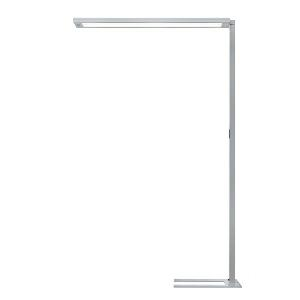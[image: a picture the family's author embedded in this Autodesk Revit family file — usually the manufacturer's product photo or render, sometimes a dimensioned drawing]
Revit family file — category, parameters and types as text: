
# Revit family: lavigo_-_dps_18000_vtl_r_g2_00801138_1d74
name_source: partatom
category: Lighting Fixtures
units: mm (PartAtom-declared; Revit-internal decimal feet)

## family parameters
Cut with Voids When Loaded = No
Host = Face
Light Source = No
Part Type = Normal
Room Calculation Point = No
Round Connector Dimension = Use Diameter
Shared = No

## types (1)
- LAVIGO - DPS 18000/VTL/R/G2 (1 x LED VTL, 18550 lm, 3000-6500K)
    Apparent Load = 128 VA
    Approval mark = CE
    CIE Flux Codes = 60 87 97 9 100
    Color Rendering = 80-89
    Color Temperature = 3000-6500K
    Control Gear = Electronic ballast
    Default Elevation = 1800 mm
    Description = DPS 18000/VTL/R/G2|Free-standing luminaire|light source: LED  3000-6500 K  Energy efficiency category A/A+/A++|LED  4000 K 4000 K Energy efficiency category A/A+/A++|work equipment: Electronic ballast DALI|connected load: 220-240 V, 50/60 Hz|Power consumption: approx. 128 W|standby: approx. 0,50|power factor: approx. 0,966|luminous flux: 18850 lm|luminous efficacy: 147 lm/W|light distribution: Direct/indirect|direct ratio: approx. 9 %|color rendering index (CRI): >= 80|technology: Presence and daylight sensor control (PIR)|operation: Multi-function switch|luminaire body|material: Steel/plastic|surface: Powder coatet|colour: White|lamp cover: Polycarbonate (PC), Clear, Structured|tubular section|material: Steel tube|surface: Powder-coated|Form: Tubular section upright|colour of tubular section: White|luminaire base|Form: C-form flat|weight (net): approx. 15.4 kg|mains lead: 3.00 m Mains plug CEE 7/VII|Fastening: Floor standing base|decorative contrast side parts: Flint grey|glare control: Prism aperture|luminance(L65): <= 2800 cd/m|unified glare rating(4H 8H): <=  16|special features: Luminaire head detachable, Cradle to Cradle Certified TM, Direct light component with edge light and light-guide technology for homogenous light exit, Flicker-free, Indirect light component biodynamic light VTL, direct light component neutral working light, Integrated light and presence sensor PIR, Integrated light management for biodynamic light VTL, Retrofittable with TALK module, Separated, direct and indirect light individually adjustable|
    Frequency = 50 Hz
    Height = 36 mm
    Lamp = 1 x LED VTL
    Lamp Light Flux = 18550 lm
    Lamp count = 1
    Length = 1265 mm
    Luminous efficacy = 145 lm/W
    Manufacturer = Waldmann
    ModVariant = No
    Model = 00801138
    Mounting Place = Floor
    Mounting Type = Freestanding
    Number of Poles = 1
    OnlyDefault = Yes
    Power Factor = 1
    Product Name = LAVIGO - DPS 18000/VTL/R/G2
    Product group = Free standing luminaire
    ProductGroupID = 13
    Protection Class = Protection class I
    Protection Degree = IP 20
    RLX_Detail_Level = 1
    RLX_Emergency_Light_Flux = 0 lm
    RLX_Emergency_Type = 0
    RLX_Emergency_Type_DB = No
    RlxData = <blob elided: 30953 chars, md5=ab62c28e>
    Socket = socket
    Standby Power = 0 W
    System Light Flux = 18550 lm
    System Power = 128 W
    Type Comments = Product without accessories
    Type Image = 121763000-00710211.jpg
    URL = http://relux.com
    VarID = ---
    Voltage = 230 V
    Voltage Range = 220-240 V
    Weight = 0.00 kg
    Width = 201 mm

## geometry (parser evidence)
native form markers: Blend x4, Sweep x14
no freeform markers — native parametric forms only
